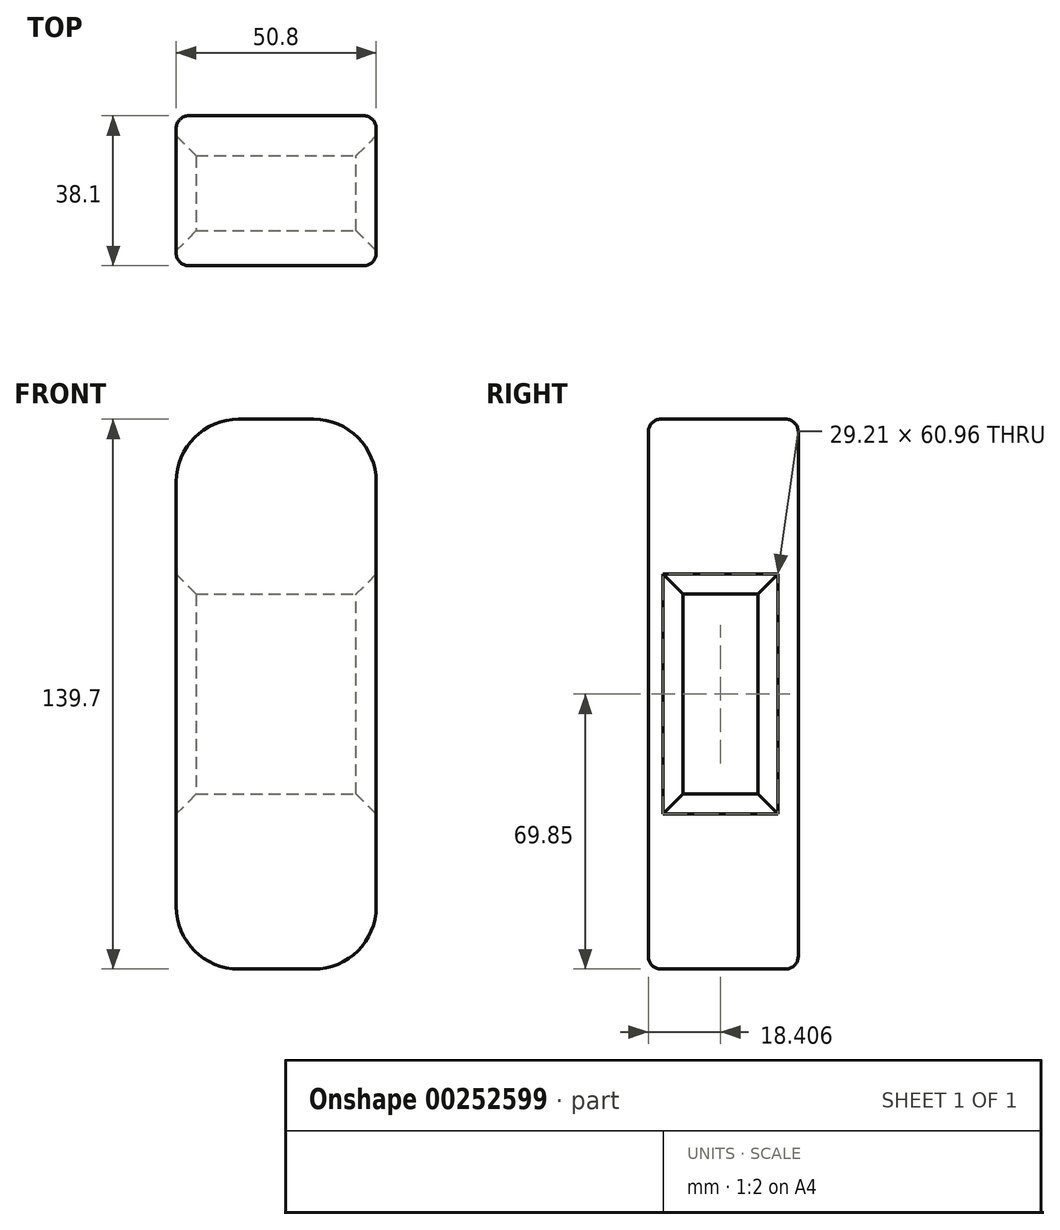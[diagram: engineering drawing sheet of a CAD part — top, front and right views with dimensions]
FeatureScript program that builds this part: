
annotation { "Feature Type Name" : "Feature", "Feature Type Description" : "" }
export const myFeature = defineFeature(function(context is Context, id is Id, definition is map)
    precondition{}
    {
        {
            var Q0;
            Q0=qCreatedBy(makeId("Front.planeOp"),FACE);
            var sketch = newSketch(context, id + "F0", { "sketchPlane" : qUnion([Q0])});
            skLineSegment(sketch, "E0.bottom", {"start": v(-9.53, 69.85) * mm, "end": v(9.52, 69.85) * mm});
            skLineSegment(sketch, "E0.top", {"start": v(-9.53, -69.85) * mm, "end": v(9.52, -69.85) * mm});
            skLineSegment(sketch, "E0.left", {"start": v(-25.4, 53.97) * mm, "end": v(-25.4, -53.98) * mm});
            skLineSegment(sketch, "E0.right", {"start": v(25.4, 53.97) * mm, "end": v(25.4, -53.98) * mm});
            skPoint(sketch, "E0.middle", {"position": v(0, 0) * mm});
            skPoint(sketch, "E1.visualSharp", {"position": v(25.4, 69.85) * mm});
            skArc(sketch, "E1.filletArc", {"start": v(25.4, 53.97) * mm, "mid": v(20.75, 65.2) * mm, "end": v(9.52, 69.85) * mm});
            skPoint(sketch, "E2.visualSharp", {"position": v(-25.4, 69.85) * mm});
            skArc(sketch, "E2.filletArc", {"start": v(-9.53, 69.85) * mm, "mid": v(-20.75, 65.2) * mm, "end": v(-25.4, 53.97) * mm});
            skPoint(sketch, "E3.visualSharp", {"position": v(25.4, -69.85) * mm});
            skArc(sketch, "E3.filletArc", {"start": v(9.52, -69.85) * mm, "mid": v(20.75, -65.2) * mm, "end": v(25.4, -53.98) * mm});
            skPoint(sketch, "E4.visualSharp", {"position": v(-25.4, -69.85) * mm});
            skArc(sketch, "E4.filletArc", {"start": v(-25.4, -53.98) * mm, "mid": v(-20.75, -65.2) * mm, "end": v(-9.53, -69.85) * mm});
            skSolve(sketch);
        }
        {
            var Q0;
            Q0=makeQuery(id+"F0.imprint","IMPRINT",FACE,{"disambiguationData":[TD([[makeQuery(id+"F0.imprint","IMPRINT",EDGE,{"derivedFrom":sQuery(id+"F0.wireOp",EDGE,"E0.bottom")}),-1.0]])]});
            extrude(context, id + "F1", {"entities" : qUnion([Q0]), "depth" : 38.1 * mm});
        }
        {
            var Q0;
            Q0=makeQuery(id+"F1.opExtrude","CAP_EDGE",EDGE,{"disambiguationData":[OSD([sQuery(id+"F0.wireOp",EDGE,"E0.right")])],"isStart":false});
            var Q1;
            Q1=makeQuery(id+"F1.opExtrude","CAP_EDGE",EDGE,{"disambiguationData":[OSD([sQuery(id+"F0.wireOp",EDGE,"E0.right")])],"isStart":true});
            fillet(context, id + "F2", {"entities" : qUnion([Q0, Q1]), "radius" : 3.17 * mm, "tangentPropagation" : true, "allowEdgeOverflow" : false});
        }
        {
            var Q0;
            Q0=makeQuery(id+"F1.opExtrude","SWEPT_FACE",FACE,{"disambiguationData":[OSD([sQuery(id+"F0.wireOp",EDGE,"E0.right")])]});
            var sketch = newSketch(context, id + "F3", { "sketchPlane" : qUnion([Q0])});
            skLineSegment(sketch, "E5.bottom", {"start": v(-10.17, -25.4) * mm, "end": v(-29.22, -25.4) * mm});
            skLineSegment(sketch, "E5.top", {"start": v(-10.17, 25.4) * mm, "end": v(-29.22, 25.4) * mm});
            skLineSegment(sketch, "E5.left", {"start": v(-10.17, -25.4) * mm, "end": v(-10.17, 25.4) * mm});
            skLineSegment(sketch, "E5.right", {"start": v(-29.22, -25.4) * mm, "end": v(-29.22, 25.4) * mm});
            skPoint(sketch, "E5.middle", {"position": v(-19.7, 0) * mm});
            skPoint(sketch, "E5.middle.positionSnap0", {"position": v(-34.93, 0) * mm});
            skPoint(sketch, "E5.centerSnap0", {"position": v(-34.93, 0) * mm});
            skSolve(sketch);
        }
        {
            var Q0;
            Q0=makeQuery(id+"F3.imprint","IMPRINT",FACE,{"disambiguationData":[TD([[makeQuery(id+"F3.imprint","IMPRINT",EDGE,{"derivedFrom":sQuery(id+"F3.wireOp",EDGE,"E5.bottom")}),-1.0]])]});
            extrude(context, id + "F4", {"entities" : qUnion([Q0]), "operationType" : NewBodyOperationType.REMOVE, "endBound" : BoundingType.THROUGH_ALL, "oppositeDirection" : true, "depth" : 25.4 * mm});
        }
        {
            var Q0;
            Q0=makeQuery(id+"F1.opExtrude","SWEPT_FACE",FACE,{"disambiguationData":[OSD([sQuery(id+"F0.wireOp",EDGE,"E0.left")])]});
            var Q1;
            Q1=makeQuery(id+"F1.opExtrude","SWEPT_FACE",FACE,{"disambiguationData":[OSD([sQuery(id+"F0.wireOp",EDGE,"E0.right")])]});
            chamfer(context, id + "F5", {"entities" : qUnion([Q0, Q1]), "width" : 5.08 * mm, "tangentPropagation" : true});
        }
    });
